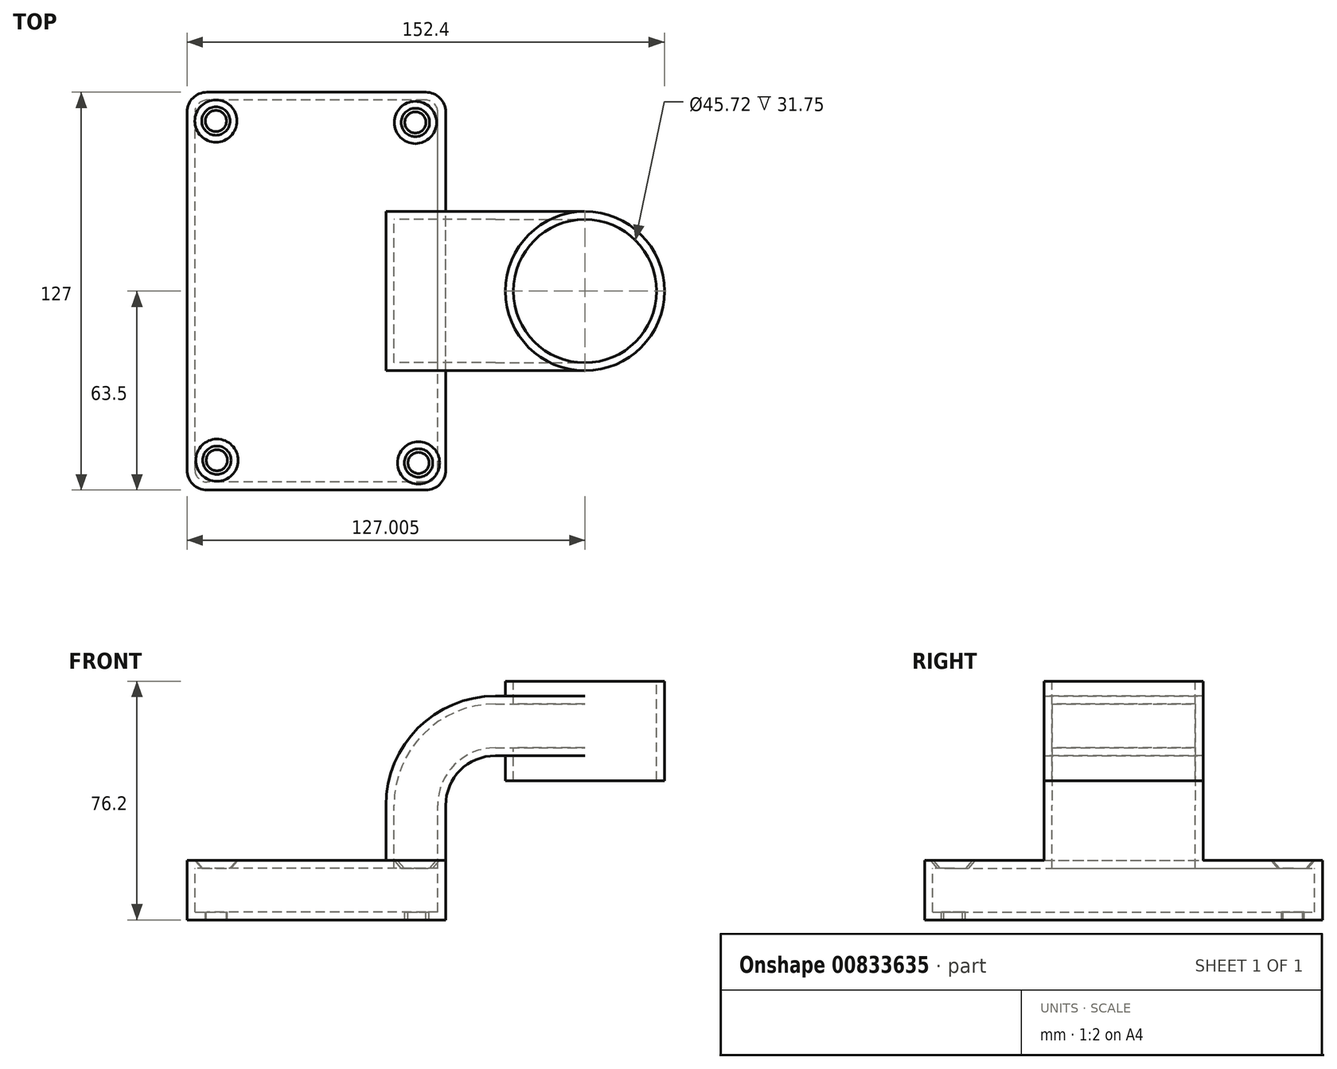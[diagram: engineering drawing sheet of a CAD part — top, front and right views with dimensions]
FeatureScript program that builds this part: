
annotation { "Feature Type Name" : "Feature", "Feature Type Description" : "" }
export const myFeature = defineFeature(function(context is Context, id is Id, definition is map)
    precondition{}
    {
        {
            var Q0;
            Q0=qCreatedBy(makeId("Front.planeOp"),FACE);
            var sketch = newSketch(context, id + "F0", { "sketchPlane" : qUnion([Q0])});
            skLineSegment(sketch, "E0.bottom", {"start": v(47.51, 7.76) * mm, "end": v(-35.04, 7.76) * mm});
            skLineSegment(sketch, "E0.top", {"start": v(47.51, 26.8) * mm, "end": v(-35.04, 26.8) * mm});
            skLineSegment(sketch, "E0.left", {"start": v(47.51, 7.76) * mm, "end": v(47.51, 26.8) * mm});
            skLineSegment(sketch, "E0.right", {"start": v(-35.04, 7.76) * mm, "end": v(-35.04, 26.8) * mm});
            skPoint(sketch, "E0.middle", {"position": v(6.24, 17.28) * mm});
            skLineSegment(sketch, "E1.bottom", {"start": v(117.36, 52.2) * mm, "end": v(66.56, 52.2) * mm});
            skLineSegment(sketch, "E1.top", {"start": v(117.36, 83.96) * mm, "end": v(66.56, 83.96) * mm});
            skLineSegment(sketch, "E1.left", {"start": v(117.36, 52.2) * mm, "end": v(117.36, 83.96) * mm});
            skLineSegment(sketch, "E1.right", {"start": v(66.56, 52.2) * mm, "end": v(66.56, 83.96) * mm});
            skPoint(sketch, "E1.middle", {"position": v(91.96, 68.08) * mm});
            skLineSegment(sketch, "E2", {"start": v(47.51, 26.8) * mm, "end": v(47.51, 44.3) * mm});
            skArc(sketch, "E3", {"start": v(47.51, 44.3) * mm, "mid": v(52.16, 55.52) * mm, "end": v(63.39, 60.17) * mm});
            skArc(sketch, "E4.1", {"start": v(28.46, 44.3) * mm, "mid": v(38.7, 68.99) * mm, "end": v(63.39, 79.22) * mm});
            skLineSegment(sketch, "E4.2", {"start": v(28.46, 26.8) * mm, "end": v(28.46, 44.3) * mm});
            skFitSpline(sketch, "E5", {"points": [v(-35.04, 26.8) * mm, v(63.39, 79.22) * mm], "startDerivative": vector(61.35, 101.74) * mm, "endDerivative": vector(117.27, -14.61) * mm});
            skLineSegment(sketch, "E6", {"start": v(91.96, 83.96) * mm, "end": v(91.96, 52.2) * mm});
            skLineSegment(sketch, "E7", {"start": v(63.39, 79.22) * mm, "end": v(91.96, 79.22) * mm});
            skLineSegment(sketch, "E8", {"start": v(63.39, 60.17) * mm, "end": v(91.96, 60.17) * mm});
            skSolve(sketch);
        }
        {
            var Q0;
            Q0=makeQuery(id+"F0.imprint","IMPRINT",FACE,{"disambiguationData":[TD([[makeQuery(id+"F0.imprint","IMPRINT",EDGE,{"derivedFrom":sQuery(id+"F0.wireOp",EDGE,"E0.bottom")}),-1.0]])]});
            extrude(context, id + "F1", {"entities" : qUnion([Q0]), "endBound" : BoundingType.SYMMETRIC, "depth" : 127 * mm, "offsetDistance" : 25.4 * mm});
        }
        {
            var Q0;
            {var subQ1=sQuery(id+"F0.wireOp",EDGE,"E2");Q0=makeQuery(id+"F0.imprint","IMPRINT",FACE,{"disambiguationData":[TD([[makeQuery(id+"F0.imprint","IMPRINT",EDGE,{"derivedFrom":subQ1}),1.0]])]});}
            var Q1;
            {var subQ0=sQuery(id+"F0.wireOp",EDGE,"E8");var subQ1=sQuery(id+"F0.wireOp",EDGE,"E1.right");var subQ2=makeQuery(id+"F0.imprint","INTERSECT",VERTEX,{"derivedFrom":[subQ1,subQ0]});Q1=makeQuery(id+"F0.imprint","IMPRINT",FACE,{"disambiguationData":[TD([[makeQuery(id+"F0.imprint","IMPRINT",EDGE,{"disambiguationData":[TD([[subQ2,-1.0]])],"derivedFrom":subQ1}),-1.0]])]});}
            extrude(context, id + "F2", {"entities" : qUnion([Q0, Q1]), "operationType" : NewBodyOperationType.ADD, "endBound" : BoundingType.SYMMETRIC, "depth" : 50.8 * mm, "offsetDistance" : 25.4 * mm});
        }
        {
            var Q0;
            Q0=makeQuery(id+"F0.imprint","IMPRINT",FACE,{"disambiguationData":[TD([[makeQuery(id+"F0.imprint","IMPRINT",EDGE,{"derivedFrom":sQuery(id+"F0.wireOp",EDGE,"E4.1")}),1.0]])]});
            extrude(context, id + "F3", {"entities" : qUnion([Q0]), "operationType" : NewBodyOperationType.ADD, "endBound" : BoundingType.SYMMETRIC, "depth" : 15.88 * mm, "offsetDistance" : 25.4 * mm});
        }
        {
            var Q0;
            {var subQ4=sQuery(id+"F0.wireOp",EDGE,"E1.left");Q0=makeQuery(id+"F0.imprint","IMPRINT",FACE,{"disambiguationData":[TD([[makeQuery(id+"F0.imprint","IMPRINT",EDGE,{"derivedFrom":subQ4}),1.0]])]});}
            var Q1;
            Q1=sQuery(id+"F0.wireOp",EDGE,"E6");
            revolve(context, id + "F4", {"operationType" : NewBodyOperationType.ADD, "surfaceOperationType" : NewSurfaceOperationType.NEW, "entities" : qUnion([Q0]), "axis" : qUnion([Q1]), "revolveType" : RevolveType.FULL});
        }
        {
            var Q0;
            Q0=makeQuery(id+"F1.opExtrude","CAP_EDGE",EDGE,{"disambiguationData":[OSD([sQuery(id+"F0.wireOp",EDGE,"E0.right")])],"isStart":false});
            var Q1;
            Q1=makeQuery(id+"F1.opExtrude","CAP_EDGE",EDGE,{"disambiguationData":[OSD([sQuery(id+"F0.wireOp",EDGE,"E0.right")])],"isStart":true});
            var Q2;
            Q2=makeQuery(id+"F1.opExtrude","CAP_EDGE",EDGE,{"disambiguationData":[OSD([sQuery(id+"F0.wireOp",EDGE,"E0.left")])],"isStart":false});
            var Q3;
            Q3=makeQuery(id+"F1.opExtrude","CAP_EDGE",EDGE,{"disambiguationData":[OSD([sQuery(id+"F0.wireOp",EDGE,"E0.left")])],"isStart":true});
            fillet(context, id + "F5", {"entities" : qUnion([Q0, Q1, Q2, Q3]), "radius" : 6.35 * mm, "tangentPropagation" : true, "allowEdgeOverflow" : false});
        }
        {
            var Q0;
            Q0=makeQuery(id+"F4.opRevolve","SWEPT_FACE",FACE,{"disambiguationData":[OSD([sQuery(id+"F0.wireOp",EDGE,"E1.top")])]});
            var Q1;
            Q1=makeQuery(id+"F4.opRevolve","SWEPT_FACE",FACE,{"disambiguationData":[OSD([sQuery(id+"F0.wireOp",EDGE,"E1.bottom")])]});
            shell(context, id + "F6", {"entities" : qUnion([Q0, Q1]), "thickness" : 2.54 * mm});
        }
        {
            var Q0;
            {var subQ3=sQuery(id+"F0.wireOp",EDGE,"E0.top");var subQ5=sQuery(id+"F0.wireOp",EDGE,"E0.right");var subQ6=sQuery(id+"F0.wireOp",EDGE,"E0.left");Q0=makeQuery(id+"F3.boolean.opBoolean","SPLIT",FACE,{"disambiguationData":[TD([makeQuery(id+"F1.opExtrude","CAP_FACE",FACE,{"disambiguationData":[OSD([sQuery(id+"F0.wireOp",EDGE,"E0.bottom"),subQ3,subQ6,subQ5])],"isStart":false})])],"derivedFrom":makeQuery(id+"F1.opExtrude","SWEPT_FACE",FACE,{"disambiguationData":[OSD([subQ3])]})});}
            var sketch = newSketch(context, id + "F7", { "sketchPlane" : qUnion([Q0])});
            skCircle(sketch, "E9", {"center": v(-25.83, 54.3) * mm, "radius": 2.86 * mm});
            skSolve(sketch);
        }
        {
            var Q0;
            Q0=sQuery(id+"F7.wireOp",VERTEX,"E9.center");
            var Q1;
            Q1=makeQuery(id+"F1.opExtrude","SWEPT_BODY",BODY,{"disambiguationData":[OSD([sQuery(id+"F0.wireOp",EDGE,"E0.bottom"),sQuery(id+"F0.wireOp",EDGE,"E0.top"),sQuery(id+"F0.wireOp",EDGE,"E0.left"),sQuery(id+"F0.wireOp",EDGE,"E0.right")])]});
            hole(context, id + "F8", {"style" : HoleStyle.C_SINK, "endStyle" : HoleEndStyle.THROUGH, "standardTappedOrClearance" : lookupTablePath({ "fit" : "Normal (ASME)", "standard" : "ANSI", "size" : "1/4", "type" : "Clearance" }), "standardBlindInLast" : lookupTablePath({ "fit" : "Free", "standard" : "ANSI", "size" : "1/4", "type" : "Clearance" }), "holeDiameter" : 6.76 * mm, "cSinkDiameter" : 13.5 * mm, "cSinkAngle" : 82 * degree, "majorDiameter" : 6.35 * mm, "isTappedThrough" : true, "tappedDepth" : 12.7 * mm, "tapClearance" : 3, "locations" : qUnion([Q0]), "scope" : qUnion([Q1])});
        }
        {
            var Q0;
            {var subQ3=sQuery(id+"F0.wireOp",EDGE,"E0.top");var subQ4=sQuery(id+"F0.wireOp",EDGE,"E0.right");var subQ5=sQuery(id+"F0.wireOp",EDGE,"E0.left");Q0=makeQuery(id+"F3.boolean.opBoolean","SPLIT",FACE,{"disambiguationData":[TD([makeQuery(id+"F1.opExtrude","CAP_FACE",FACE,{"disambiguationData":[OSD([sQuery(id+"F0.wireOp",EDGE,"E0.bottom"),subQ3,subQ5,subQ4])],"isStart":true})])],"derivedFrom":makeQuery(id+"F1.opExtrude","SWEPT_FACE",FACE,{"disambiguationData":[OSD([subQ3])]})});}
            var sketch = newSketch(context, id + "F9", { "sketchPlane" : qUnion([Q0])});
            skCircle(sketch, "E10", {"center": v(37.85, 53.83) * mm, "radius": 3.32 * mm});
            skSolve(sketch);
        }
        {
            var Q0;
            Q0=sQuery(id+"F9.wireOp",VERTEX,"E10.center");
            var Q1;
            Q1=makeQuery(id+"F1.opExtrude","SWEPT_BODY",BODY,{"disambiguationData":[OSD([sQuery(id+"F0.wireOp",EDGE,"E0.bottom"),sQuery(id+"F0.wireOp",EDGE,"E0.top"),sQuery(id+"F0.wireOp",EDGE,"E0.left"),sQuery(id+"F0.wireOp",EDGE,"E0.right")])]});
            hole(context, id + "F10", {"style" : HoleStyle.C_SINK, "endStyle" : HoleEndStyle.THROUGH, "standardTappedOrClearance" : lookupTablePath({ "fit" : "Normal (ASME)", "standard" : "ANSI", "size" : "1/4", "type" : "Clearance" }), "standardBlindInLast" : lookupTablePath({ "fit" : "Free", "standard" : "ANSI", "size" : "1/4", "type" : "Clearance" }), "holeDiameter" : 6.76 * mm, "cSinkDiameter" : 13.5 * mm, "cSinkAngle" : 82 * degree, "majorDiameter" : 6.35 * mm, "isTappedThrough" : true, "tappedDepth" : 12.7 * mm, "tapClearance" : 3, "locations" : qUnion([Q0]), "scope" : qUnion([Q1])});
        }
        {
            var Q0;
            {var subQ3=sQuery(id+"F0.wireOp",EDGE,"E0.top");var subQ5=sQuery(id+"F0.wireOp",EDGE,"E0.right");var subQ6=sQuery(id+"F0.wireOp",EDGE,"E0.left");Q0=makeQuery(id+"F3.boolean.opBoolean","SPLIT",FACE,{"disambiguationData":[TD([makeQuery(id+"F1.opExtrude","CAP_FACE",FACE,{"disambiguationData":[OSD([sQuery(id+"F0.wireOp",EDGE,"E0.bottom"),subQ3,subQ6,subQ5])],"isStart":false})])],"derivedFrom":makeQuery(id+"F1.opExtrude","SWEPT_FACE",FACE,{"disambiguationData":[OSD([subQ3])]})});}
            var sketch = newSketch(context, id + "F11", { "sketchPlane" : qUnion([Q0])});
            skCircle(sketch, "E11", {"center": v(-25.51, -53.98) * mm, "radius": 3.18 * mm});
            skSolve(sketch);
        }
        {
            var Q0;
            Q0=sQuery(id+"F11.wireOp",VERTEX,"E11.center");
            var Q1;
            Q1=makeQuery(id+"F1.opExtrude","SWEPT_BODY",BODY,{"disambiguationData":[OSD([sQuery(id+"F0.wireOp",EDGE,"E0.bottom"),sQuery(id+"F0.wireOp",EDGE,"E0.top"),sQuery(id+"F0.wireOp",EDGE,"E0.left"),sQuery(id+"F0.wireOp",EDGE,"E0.right")])]});
            hole(context, id + "F12", {"style" : HoleStyle.C_SINK, "endStyle" : HoleEndStyle.THROUGH, "standardTappedOrClearance" : lookupTablePath({ "fit" : "Normal (ASME)", "standard" : "ANSI", "size" : "1/4", "type" : "Clearance" }), "standardBlindInLast" : lookupTablePath({ "fit" : "Free", "standard" : "ANSI", "size" : "1/4", "type" : "Clearance" }), "holeDiameter" : 6.76 * mm, "cSinkDiameter" : 13.5 * mm, "cSinkAngle" : 82 * degree, "majorDiameter" : 6.35 * mm, "isTappedThrough" : true, "tappedDepth" : 12.7 * mm, "tapClearance" : 3, "locations" : qUnion([Q0]), "scope" : qUnion([Q1])});
        }
        {
            var Q0;
            {var subQ3=sQuery(id+"F0.wireOp",EDGE,"E0.top");var subQ5=sQuery(id+"F0.wireOp",EDGE,"E0.right");var subQ6=sQuery(id+"F0.wireOp",EDGE,"E0.left");Q0=makeQuery(id+"F3.boolean.opBoolean","SPLIT",FACE,{"disambiguationData":[TD([makeQuery(id+"F1.opExtrude","CAP_FACE",FACE,{"disambiguationData":[OSD([sQuery(id+"F0.wireOp",EDGE,"E0.bottom"),subQ3,subQ6,subQ5])],"isStart":false})])],"derivedFrom":makeQuery(id+"F1.opExtrude","SWEPT_FACE",FACE,{"disambiguationData":[OSD([subQ3])]})});}
            var sketch = newSketch(context, id + "F13", { "sketchPlane" : qUnion([Q0])});
            skCircle(sketch, "E12", {"center": v(38.85, -54.84) * mm, "radius": 2.31 * mm});
            skSolve(sketch);
        }
        {
            var Q0;
            Q0=sQuery(id+"F13.wireOp",VERTEX,"E12.center");
            var Q1;
            Q1=makeQuery(id+"F1.opExtrude","SWEPT_BODY",BODY,{"disambiguationData":[OSD([sQuery(id+"F0.wireOp",EDGE,"E0.bottom"),sQuery(id+"F0.wireOp",EDGE,"E0.top"),sQuery(id+"F0.wireOp",EDGE,"E0.left"),sQuery(id+"F0.wireOp",EDGE,"E0.right")])]});
            hole(context, id + "F14", {"style" : HoleStyle.C_SINK, "endStyle" : HoleEndStyle.THROUGH, "standardTappedOrClearance" : lookupTablePath({ "fit" : "Normal (ASME)", "standard" : "ANSI", "size" : "1/4", "type" : "Clearance" }), "standardBlindInLast" : lookupTablePath({ "fit" : "Free", "standard" : "ANSI", "size" : "1/4", "type" : "Clearance" }), "holeDiameter" : 6.76 * mm, "cSinkDiameter" : 13.5 * mm, "cSinkAngle" : 82 * degree, "majorDiameter" : 6.35 * mm, "isTappedThrough" : true, "tappedDepth" : 12.7 * mm, "tapClearance" : 3, "locations" : qUnion([Q0]), "scope" : qUnion([Q1])});
        }
    });
